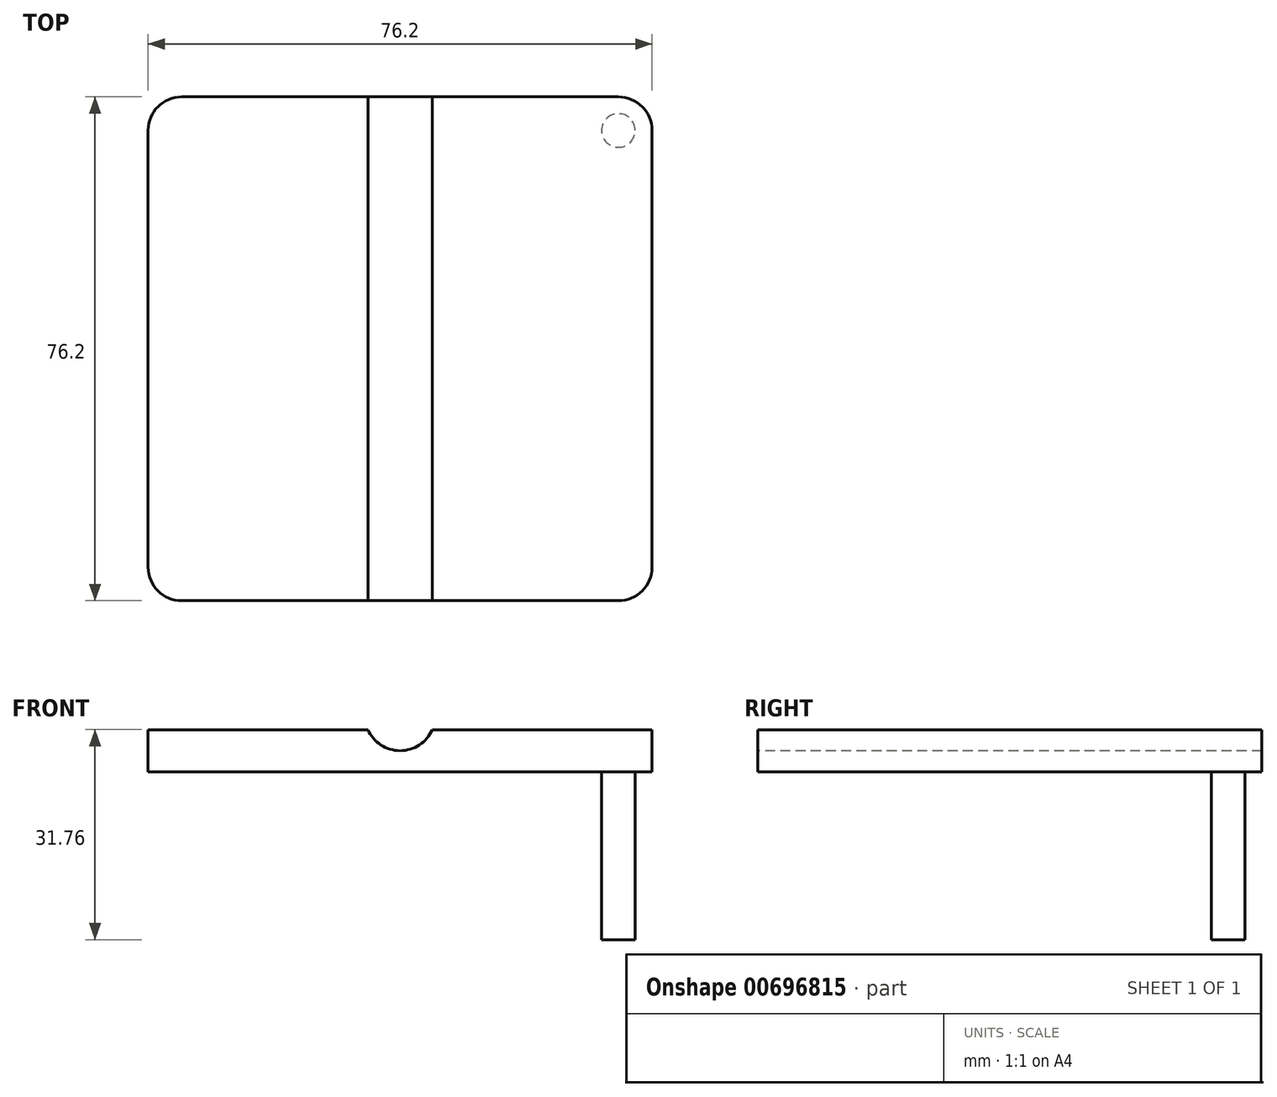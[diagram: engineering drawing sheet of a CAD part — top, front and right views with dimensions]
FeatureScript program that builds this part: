
annotation { "Feature Type Name" : "Feature", "Feature Type Description" : "" }
export const myFeature = defineFeature(function(context is Context, id is Id, definition is map)
    precondition{}
    {
        {
            var Q0;
            Q0=qCreatedBy(makeId("Top.planeOp"),FACE);
            var sketch = newSketch(context, id + "F0", { "sketchPlane" : qUnion([Q0])});
            skLineSegment(sketch, "E0.bottom", {"start": v(38.1, -38.1) * mm, "end": v(-38.1, -38.1) * mm});
            skLineSegment(sketch, "E0.top", {"start": v(38.1, 38.1) * mm, "end": v(-38.1, 38.1) * mm});
            skLineSegment(sketch, "E0.left", {"start": v(38.1, -38.1) * mm, "end": v(38.1, 38.1) * mm});
            skLineSegment(sketch, "E0.right", {"start": v(-38.1, -38.1) * mm, "end": v(-38.1, 38.1) * mm});
            skPoint(sketch, "E0.middle", {"position": v(0, 0) * mm});
            skSolve(sketch);
        }
        {
            var Q0;
            Q0=makeQuery(id+"F0.imprint","IMPRINT",FACE,{"disambiguationData":[TD([[makeQuery(id+"F0.imprint","IMPRINT",EDGE,{"derivedFrom":sQuery(id+"F0.wireOp",EDGE,"E0.bottom")}),-1.0]])]});
            extrude(context, id + "F1", {"entities" : qUnion([Q0]), "endBound" : BoundingType.SYMMETRIC, "depth" : 6.35 * mm, "offsetDistance" : 25.4 * mm});
        }
        {
            var Q0;
            Q0=makeQuery(id+"F1.opExtrude","SWEPT_EDGE",EDGE,{"disambiguationData":[OSD([sQuery(id+"F0.wireOp",EDGE,"E0.bottom"),sQuery(id+"F0.wireOp",EDGE,"E0.left")])]});
            var Q1;
            Q1=makeQuery(id+"F1.opExtrude","SWEPT_EDGE",EDGE,{"disambiguationData":[OSD([sQuery(id+"F0.wireOp",EDGE,"E0.top"),sQuery(id+"F0.wireOp",EDGE,"E0.left")])]});
            var Q2;
            Q2=makeQuery(id+"F1.opExtrude","SWEPT_EDGE",EDGE,{"disambiguationData":[OSD([sQuery(id+"F0.wireOp",EDGE,"E0.top"),sQuery(id+"F0.wireOp",EDGE,"E0.right")])]});
            var Q3;
            Q3=makeQuery(id+"F1.opExtrude","SWEPT_EDGE",EDGE,{"disambiguationData":[OSD([sQuery(id+"F0.wireOp",EDGE,"E0.bottom"),sQuery(id+"F0.wireOp",EDGE,"E0.right")])]});
            fillet(context, id + "F2", {"entities" : qUnion([Q0, Q1, Q2, Q3]), "radius" : 5.08 * mm, "tangentPropagation" : true, "allowEdgeOverflow" : false});
        }
        {
            var Q0;
            Q0=makeQuery(id+"F1.opExtrude","SWEPT_FACE",FACE,{"disambiguationData":[OSD([sQuery(id+"F0.wireOp",EDGE,"E0.bottom")])]});
            var sketch = newSketch(context, id + "F3", { "sketchPlane" : qUnion([Q0])});
            skArc(sketch, "E1", {"start": v(-4.87, 3.17) * mm, "mid": v(0, 0) * mm, "end": v(4.88, 3.18) * mm});
            skSolve(sketch);
        }
        {
            var Q0;
            {var subQ0=sQuery(id+"F3.wireOp",EDGE,"E1");Q0=makeQuery(id+"F3.imprint","IMPRINT",FACE,{"disambiguationData":[TD([[makeQuery(id+"F3.imprint","IMPRINT",EDGE,{"derivedFrom":subQ0}),1.0]])]});}
            extrude(context, id + "F4", {"entities" : qUnion([Q0]), "operationType" : NewBodyOperationType.REMOVE, "endBound" : BoundingType.THROUGH_ALL, "oppositeDirection" : true, "depth" : 76.2 * mm, "offsetDistance" : 25.4 * mm});
        }
        {
            var Q0;
            Q0=makeQuery(id+"F1.opExtrude","CAP_FACE",FACE,{"disambiguationData":[OSD([sQuery(id+"F0.wireOp",EDGE,"E0.bottom"),sQuery(id+"F0.wireOp",EDGE,"E0.top"),sQuery(id+"F0.wireOp",EDGE,"E0.left"),sQuery(id+"F0.wireOp",EDGE,"E0.right")])],"isStart":true});
            var sketch = newSketch(context, id + "F5", { "sketchPlane" : qUnion([Q0])});
            skCircle(sketch, "E2", {"center": v(33.02, -33.02) * mm, "radius": 2.54 * mm});
            skSolve(sketch);
        }
        {
            var Q0;
            Q0=makeQuery(id+"F5.imprint","IMPRINT",FACE,{"disambiguationData":[TD([[makeQuery(id+"F5.imprint","IMPRINT",EDGE,{"derivedFrom":sQuery(id+"F5.wireOp",EDGE,"E2")}),1.0]])]});
            extrude(context, id + "F6", {"entities" : qUnion([Q0]), "operationType" : NewBodyOperationType.ADD, "depth" : 25.4 * mm, "offsetDistance" : 25.4 * mm});
        }
    });
